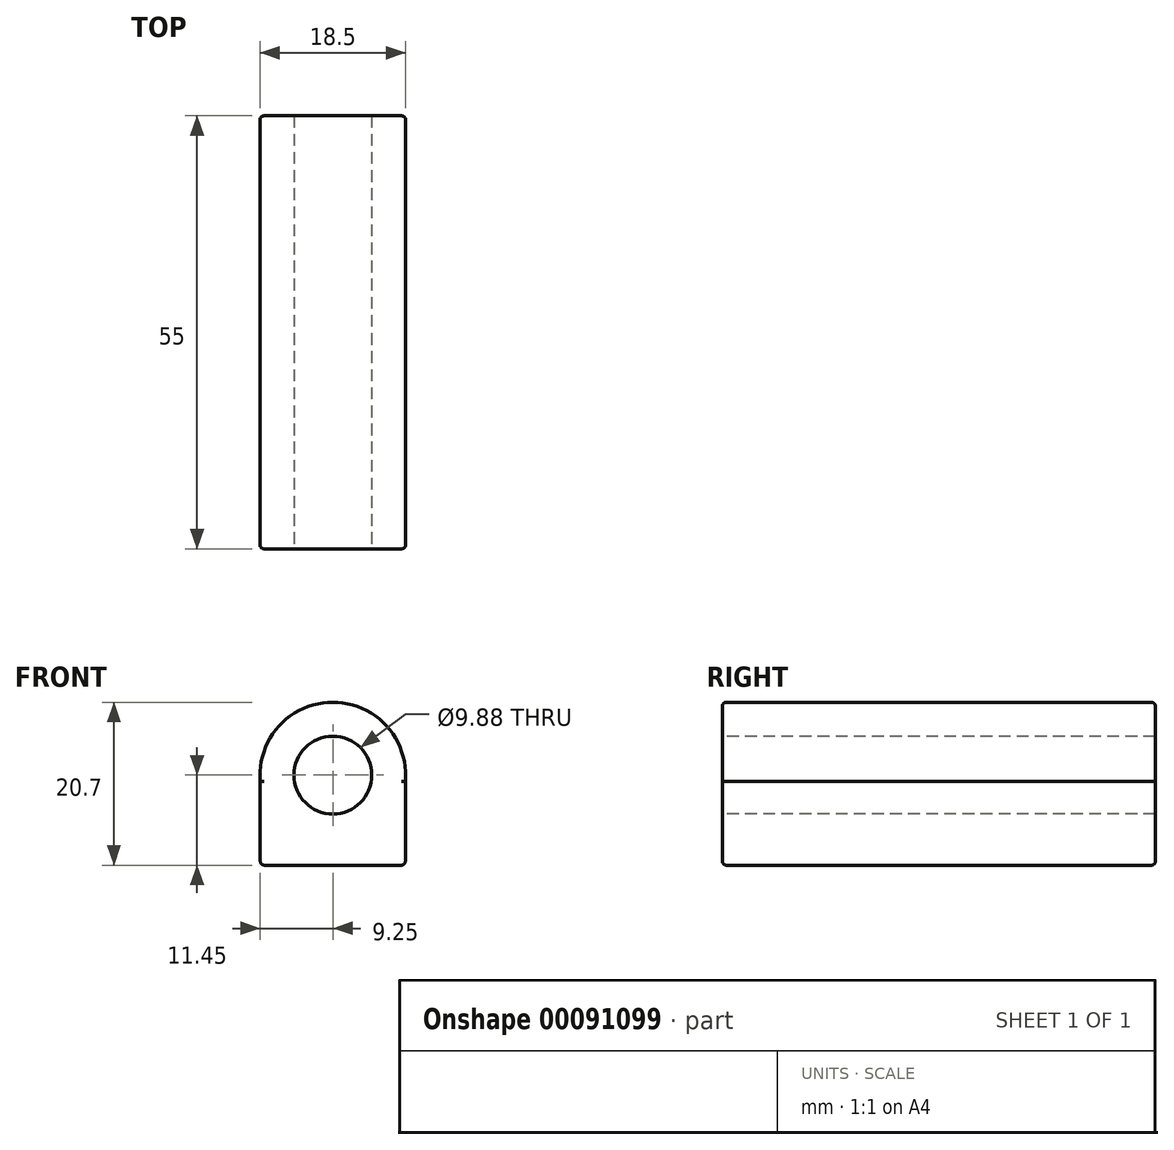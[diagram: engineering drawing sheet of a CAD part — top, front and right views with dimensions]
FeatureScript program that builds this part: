
annotation { "Feature Type Name" : "Feature", "Feature Type Description" : "" }
export const myFeature = defineFeature(function(context is Context, id is Id, definition is map)
    precondition{}
    {
        {
            var Q0;
            Q0=qCreatedBy(makeId("Front.planeOp"),FACE);
            var sketch = newSketch(context, id + "F0", { "sketchPlane" : qUnion([Q0])});
            skCircle(sketch, "E0", {"center": v(0, 0) * mm, "radius": 9.25 * mm});
            skLineSegment(sketch, "E1", {"start": v(0, 0) * mm, "end": v(0, -9.25) * mm, "construction": true});
            skLineSegment(sketch, "E2", {"start": v(0, -4.62) * mm, "end": v(-8.01, -4.62) * mm, "construction": true});
            skLineSegment(sketch, "E3.bottom", {"start": v(9.21, -9.45) * mm, "end": v(-9.21, -9.45) * mm});
            skLineSegment(sketch, "E3.top", {"start": v(9.21, 0.2) * mm, "end": v(-9.21, 0.2) * mm});
            skLineSegment(sketch, "E3.left", {"start": v(9.21, -9.45) * mm, "end": v(9.21, 0.2) * mm});
            skLineSegment(sketch, "E3.right", {"start": v(-9.21, -9.45) * mm, "end": v(-9.21, 0.2) * mm});
            skPoint(sketch, "E3.middle", {"position": v(0, -4.62) * mm});
            skSolve(sketch);
        }
        {
            var Q0;
            {var subQ5=sQuery(id+"F0.wireOp",EDGE,"E3.top");Q0=makeQuery(id+"F0.imprint","IMPRINT",FACE,{"disambiguationData":[TD([[makeQuery(id+"F0.imprint","IMPRINT",EDGE,{"derivedFrom":subQ5}),-1.0]])]});}
            var sketch = newSketch(context, id + "F1", { "sketchPlane" : qUnion([Q0])});
            skCircle(sketch, "E4", {"center": v(0, 0) * mm, "radius": 4.94 * mm});
            skSolve(sketch);
        }
        {
            var Q0;
            Q0=qSketchRegion(id+"F1",true);
            var Q1;
            {var subQ5=sQuery(id+"F0.wireOp",EDGE,"E3.top");Q1=makeQuery(id+"F0.imprint","IMPRINT",FACE,{"disambiguationData":[TD([[makeQuery(id+"F0.imprint","IMPRINT",EDGE,{"derivedFrom":subQ5}),-1.0]])]});}
            var Q2;
            {var subQ5=sQuery(id+"F0.wireOp",EDGE,"E3.top");Q2=makeQuery(id+"F0.imprint","IMPRINT",FACE,{"disambiguationData":[TD([[makeQuery(id+"F0.imprint","IMPRINT",EDGE,{"derivedFrom":subQ5}),1.0]])]});}
            var Q3;
            {var subQ5=sQuery(id+"F0.wireOp",EDGE,"E3.bottom");Q3=makeQuery(id+"F0.imprint","IMPRINT",FACE,{"disambiguationData":[TD([[makeQuery(id+"F0.imprint","IMPRINT",EDGE,{"derivedFrom":subQ5}),-1.0]])]});}
            extrude(context, id + "F2", {"entities" : qUnion([Q0, Q1, Q2, Q3]), "depth" : 55 * mm});
        }
        {
            var Q0;
            Q0=makeQuery(id+"F2.opExtrude","CAP_FACE",FACE,{"disambiguationData":[OSD([sQuery(id+"F1.wireOp",EDGE,"E4")])],"isStart":false});
            extrude(context, id + "F3", {"entities" : qUnion([Q0]), "operationType" : NewBodyOperationType.REMOVE, "endBound" : BoundingType.THROUGH_ALL, "oppositeDirection" : true, "depth" : 25 * mm});
        }
        {
            var Q0;
            Q0=makeQuery(id+"F2.opExtrude","SWEPT_FACE",FACE,{"disambiguationData":[OSD([sQuery(id+"F0.wireOp",EDGE,"E3.bottom")])]});
            extrude(context, id + "F4", {"entities" : qUnion([Q0]), "operationType" : NewBodyOperationType.ADD, "depth" : 2 * mm});
        }
        {
            var Q0;
            Q0=makeQuery(id+"F2.opExtrude","CAP_EDGE",EDGE,{"disambiguationData":[OSD([sQuery(id+"F0.wireOp",EDGE,"E0")])],"isStart":false});
            var Q1;
            Q1=makeQuery(id+"F2.opExtrude","CAP_EDGE",EDGE,{"disambiguationData":[OSD([sQuery(id+"F0.wireOp",EDGE,"E3.right")])],"isStart":false});
            var Q2;
            Q2=makeQuery(id+"F2.opExtrude","CAP_EDGE",EDGE,{"disambiguationData":[OSD([sQuery(id+"F0.wireOp",EDGE,"E3.left")])],"isStart":false});
            var Q3;
            Q3=makeQuery(id+"F2.opExtrude","CAP_EDGE",EDGE,{"disambiguationData":[OSD([sQuery(id+"F0.wireOp",EDGE,"E3.bottom")])],"isStart":false});
            var Q4;
            Q4=makeQuery(id+"F2.opExtrude","CAP_EDGE",EDGE,{"disambiguationData":[OSD([sQuery(id+"F0.wireOp",EDGE,"E3.bottom")])],"isStart":true});
            var Q5;
            Q5=makeQuery(id+"F2.opExtrude","CAP_EDGE",EDGE,{"disambiguationData":[OSD([sQuery(id+"F0.wireOp",EDGE,"E3.left")])],"isStart":true});
            var Q6;
            Q6=makeQuery(id+"F2.opExtrude","CAP_EDGE",EDGE,{"disambiguationData":[OSD([sQuery(id+"F0.wireOp",EDGE,"E3.right")])],"isStart":true});
            var Q7;
            Q7=makeQuery(id+"F2.opExtrude","CAP_EDGE",EDGE,{"disambiguationData":[OSD([sQuery(id+"F0.wireOp",EDGE,"E0")])],"isStart":true});
            var Q8;
            Q8=makeQuery(id+"F2.opExtrude","SWEPT_EDGE",EDGE,{"disambiguationData":[OSD([sQuery(id+"F0.wireOp",EDGE,"E3.bottom"),sQuery(id+"F0.wireOp",EDGE,"E3.right")])]});
            var Q9;
            Q9=makeQuery(id+"F2.opExtrude","SWEPT_EDGE",EDGE,{"disambiguationData":[OSD([sQuery(id+"F0.wireOp",EDGE,"E3.bottom"),sQuery(id+"F0.wireOp",EDGE,"E3.left")])]});
            fillet(context, id + "F5", {"entities" : qUnion([Q0, Q1, Q2, Q3, Q4, Q5, Q6, Q7, Q8, Q9]), "radius" : .5 * mm, "tangentPropagation" : true, "allowEdgeOverflow" : false});
        }
        {
            var Q0;
            Q0=makeQuery(id+"F4.opExtrude","CAP_EDGE",EDGE,{"disambiguationData":[OSD([sQuery(id+"F0.wireOp",EDGE,"E3.bottom"),sQuery(id+"F0.wireOp",EDGE,"E3.left")])],"isStart":false});
            var Q1;
            {var subQ0=sQuery(id+"F0.wireOp",EDGE,"E3.bottom");Q1=makeQuery(id+"F4.opExtrude","CAP_EDGE",EDGE,{"disambiguationData":[OSD([subQ0]),TDD([makeQuery(id+"F2.opExtrude","CAP_EDGE",EDGE,{"disambiguationData":[OSD([subQ0])],"isStart":true})])],"isStart":false});}
            var Q2;
            {var subQ0=sQuery(id+"F0.wireOp",EDGE,"E3.bottom");Q2=makeQuery(id+"F4.opExtrude","CAP_EDGE",EDGE,{"disambiguationData":[OSD([subQ0]),TDD([makeQuery(id+"F2.opExtrude","CAP_EDGE",EDGE,{"disambiguationData":[OSD([subQ0])],"isStart":false})])],"isStart":false});}
            var Q3;
            Q3=makeQuery(id+"F4.opExtrude","CAP_EDGE",EDGE,{"disambiguationData":[OSD([sQuery(id+"F0.wireOp",EDGE,"E3.bottom"),sQuery(id+"F0.wireOp",EDGE,"E3.right")])],"isStart":false});
            fillet(context, id + "F6", {"entities" : qUnion([Q0, Q1, Q2, Q3]), "radius" : .5 * mm, "tangentPropagation" : true, "allowEdgeOverflow" : false});
        }
    });
